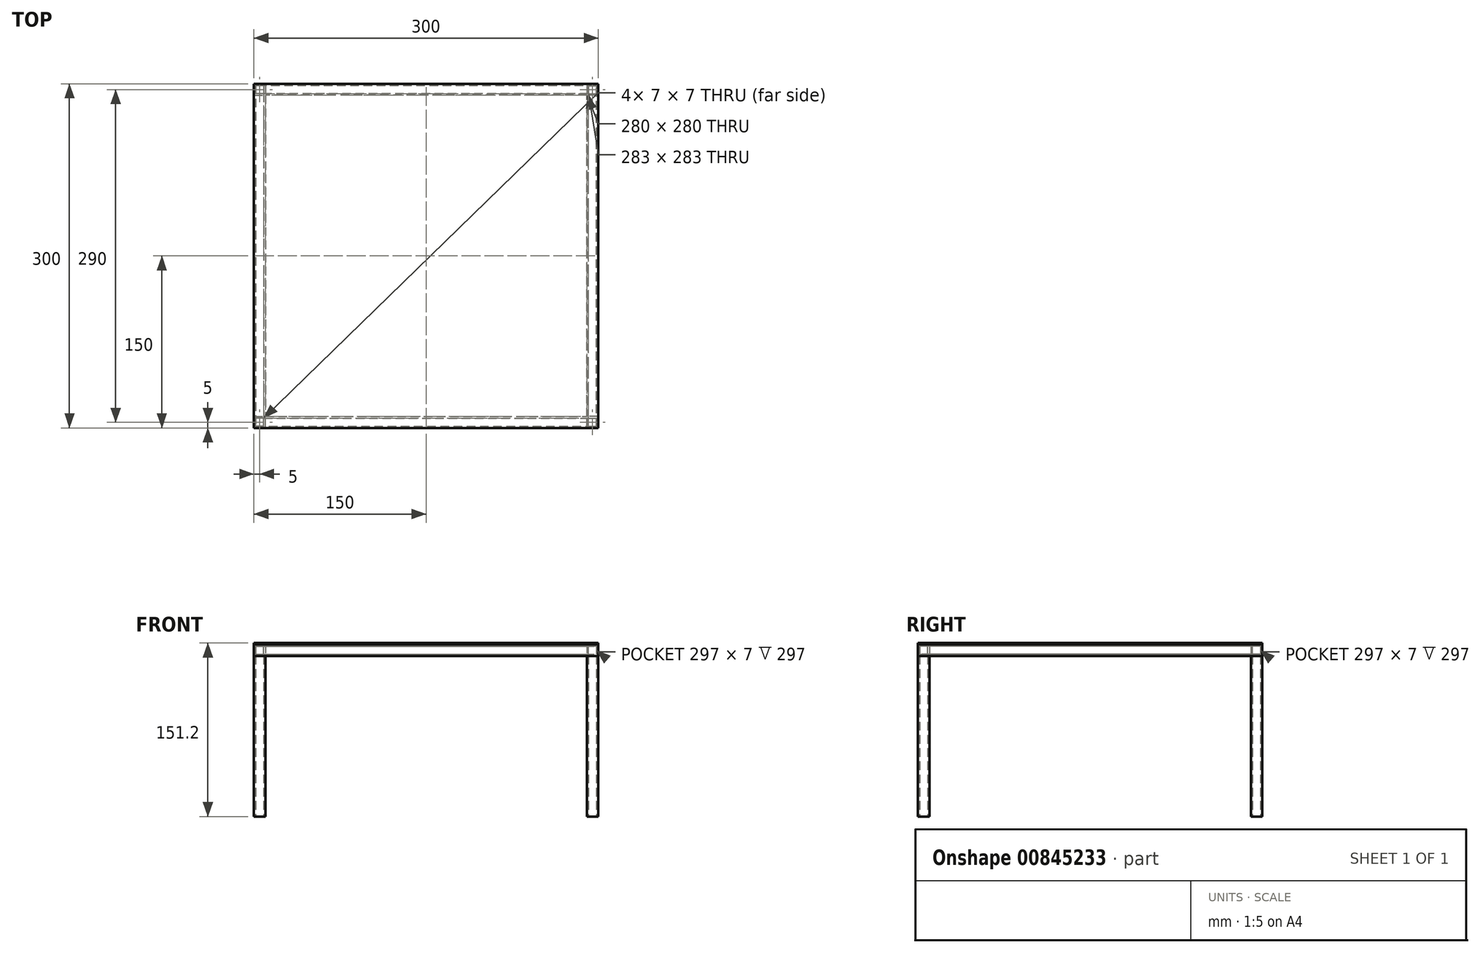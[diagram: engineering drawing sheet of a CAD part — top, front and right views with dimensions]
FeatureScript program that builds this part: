
annotation { "Feature Type Name" : "Feature", "Feature Type Description" : "" }
export const myFeature = defineFeature(function(context is Context, id is Id, definition is map)
    precondition{}
    {
        {
            var Q0;
            Q0=qCreatedBy(makeId("Top.planeOp"),FACE);
            var sketch = newSketch(context, id + "F0", { "sketchPlane" : qUnion([Q0])});
            skLineSegment(sketch, "E0.bottom", {"start": v(-150, 150) * mm, "end": v(-140, 150) * mm});
            skLineSegment(sketch, "E0.top", {"start": v(-150, 140) * mm, "end": v(-140, 140) * mm});
            skLineSegment(sketch, "E0.left", {"start": v(-150, 150) * mm, "end": v(-150, 140) * mm});
            skLineSegment(sketch, "E0.right", {"start": v(-140, 150) * mm, "end": v(-140, 140) * mm});
            skLineSegment(sketch, "E1.bottom", {"start": v(-141.5, 148.5) * mm, "end": v(-148.5, 148.5) * mm});
            skLineSegment(sketch, "E1.top", {"start": v(-141.5, 141.5) * mm, "end": v(-148.5, 141.5) * mm});
            skLineSegment(sketch, "E1.left", {"start": v(-141.5, 148.5) * mm, "end": v(-141.5, 141.5) * mm});
            skLineSegment(sketch, "E1.right", {"start": v(-148.5, 148.5) * mm, "end": v(-148.5, 141.5) * mm});
            skPoint(sketch, "E1.middle", {"position": v(-145, 145) * mm});
            skPoint(sketch, "E1.middle.positionSnap0", {"position": v(-145, 150) * mm});
            skPoint(sketch, "E1.middle.positionSnap1", {"position": v(-150, 145) * mm});
            skPoint(sketch, "E1.centerSnap0", {"position": v(-145, 150) * mm});
            skPoint(sketch, "E1.centerSnap1", {"position": v(-150, 145) * mm});
            skLineSegment(sketch, "E2.MirrorCS", {"start": v(150, 150) * mm, "end": v(140, 150) * mm});
            skLineSegment(sketch, "E3.MirrorCS", {"start": v(148.5, 148.5) * mm, "end": v(148.5, 141.5) * mm});
            skLineSegment(sketch, "E4.MirrorCS", {"start": v(150, 150) * mm, "end": v(150, 140) * mm});
            skLineSegment(sketch, "E5.MirrorCS", {"start": v(141.5, 148.5) * mm, "end": v(148.5, 148.5) * mm});
            skPoint(sketch, "E6.MirrorP", {"position": v(145, 150) * mm});
            skPoint(sketch, "E7.MirrorP", {"position": v(150, 145) * mm});
            skLineSegment(sketch, "E8.MirrorCS", {"start": v(141.5, 148.5) * mm, "end": v(141.5, 141.5) * mm});
            skLineSegment(sketch, "E9.MirrorCS", {"start": v(150, 140) * mm, "end": v(140, 140) * mm});
            skPoint(sketch, "E10.MirrorP", {"position": v(145, 145) * mm});
            skLineSegment(sketch, "E11.MirrorCS", {"start": v(140, 150) * mm, "end": v(140, 140) * mm});
            skLineSegment(sketch, "E12.MirrorCS", {"start": v(141.5, 141.5) * mm, "end": v(148.5, 141.5) * mm});
            skLineSegment(sketch, "E13.MirrorCS", {"start": v(141.5, -148.5) * mm, "end": v(141.5, -141.5) * mm});
            skLineSegment(sketch, "E14.MirrorCS", {"start": v(141.5, -148.5) * mm, "end": v(148.5, -148.5) * mm});
            skLineSegment(sketch, "E15.MirrorCS", {"start": v(140, -150) * mm, "end": v(140, -140) * mm});
            skLineSegment(sketch, "E16.MirrorCS", {"start": v(-141.5, -141.5) * mm, "end": v(-148.5, -141.5) * mm});
            skLineSegment(sketch, "E17.MirrorCS", {"start": v(-150, -150) * mm, "end": v(-140, -150) * mm});
            skLineSegment(sketch, "E18.MirrorCS", {"start": v(-150, -140) * mm, "end": v(-140, -140) * mm});
            skLineSegment(sketch, "E19.MirrorCS", {"start": v(-150, -150) * mm, "end": v(-150, -140) * mm});
            skLineSegment(sketch, "E20.MirrorCS", {"start": v(-148.5, -148.5) * mm, "end": v(-148.5, -141.5) * mm});
            skLineSegment(sketch, "E21.MirrorCS", {"start": v(-141.5, -148.5) * mm, "end": v(-141.5, -141.5) * mm});
            skLineSegment(sketch, "E22.MirrorCS", {"start": v(-141.5, -148.5) * mm, "end": v(-148.5, -148.5) * mm});
            skLineSegment(sketch, "E23.MirrorCS", {"start": v(150, -150) * mm, "end": v(140, -150) * mm});
            skLineSegment(sketch, "E24.MirrorCS", {"start": v(150, -150) * mm, "end": v(150, -140) * mm});
            skLineSegment(sketch, "E25.MirrorCS", {"start": v(148.5, -148.5) * mm, "end": v(148.5, -141.5) * mm});
            skLineSegment(sketch, "E26.MirrorCS", {"start": v(-140, -150) * mm, "end": v(-140, -140) * mm});
            skPoint(sketch, "E27.MirrorP", {"position": v(145, -150) * mm});
            skLineSegment(sketch, "E28.MirrorCS", {"start": v(150, -140) * mm, "end": v(140, -140) * mm});
            skLineSegment(sketch, "E29.MirrorCS", {"start": v(141.5, -141.5) * mm, "end": v(148.5, -141.5) * mm});
            skPoint(sketch, "E30.MirrorP", {"position": v(150, -145) * mm});
            skPoint(sketch, "E31.MirrorP", {"position": v(-145, -150) * mm});
            skPoint(sketch, "E32.MirrorP", {"position": v(-150, -145) * mm});
            skPoint(sketch, "E33.MirrorP", {"position": v(-145, -145) * mm});
            skPoint(sketch, "E34.MirrorP", {"position": v(145, -145) * mm});
            skSolve(sketch);
        }
        {
            var Q0;
            Q0=qSketchRegion(id+"F0",true);
            extrude(context, id + "F1", {"entities" : qUnion([Q0]), "depth" : 140 * mm, "offsetDistance" : 25 * mm});
        }
        {
            var Q0;
            Q0=makeQuery(id+"F1.opExtrude","CAP_FACE",FACE,{"disambiguationData":[OSD([sQuery(id+"F0.wireOp",EDGE,"E16.MirrorCS"),sQuery(id+"F0.wireOp",EDGE,"E17.MirrorCS"),sQuery(id+"F0.wireOp",EDGE,"E18.MirrorCS"),sQuery(id+"F0.wireOp",EDGE,"E19.MirrorCS"),sQuery(id+"F0.wireOp",EDGE,"E20.MirrorCS"),sQuery(id+"F0.wireOp",EDGE,"E21.MirrorCS"),sQuery(id+"F0.wireOp",EDGE,"E22.MirrorCS"),sQuery(id+"F0.wireOp",EDGE,"E26.MirrorCS")])],"isStart":false});
            var sketch = newSketch(context, id + "F2", { "sketchPlane" : qUnion([Q0])});
            skLineSegment(sketch, "E35.bottom", {"start": v(-150, 150) * mm, "end": v(150, 150) * mm});
            skLineSegment(sketch, "E35.top", {"start": v(-150, -150) * mm, "end": v(150, -150) * mm});
            skLineSegment(sketch, "E35.left", {"start": v(-150, 150) * mm, "end": v(-150, -150) * mm});
            skLineSegment(sketch, "E35.right", {"start": v(150, 150) * mm, "end": v(150, -150) * mm});
            skSolve(sketch);
        }
        {
            var Q0;
            Q0=qCreatedBy(makeId("Right.planeOp"),FACE);
            var sketch = newSketch(context, id + "F3", { "sketchPlane" : qUnion([Q0])});
            skLineSegment(sketch, "E36.bottom", {"start": v(-150, 140) * mm, "end": v(-140, 140) * mm});
            skLineSegment(sketch, "E36.top", {"start": v(-150, 150) * mm, "end": v(-140, 150) * mm});
            skLineSegment(sketch, "E36.left", {"start": v(-150, 140) * mm, "end": v(-150, 150) * mm});
            skLineSegment(sketch, "E36.right", {"start": v(-140, 140) * mm, "end": v(-140, 150) * mm});
            skLineSegment(sketch, "E37.bottom", {"start": v(-141.5, 148.5) * mm, "end": v(-148.5, 148.5) * mm});
            skLineSegment(sketch, "E37.top", {"start": v(-141.5, 141.5) * mm, "end": v(-148.5, 141.5) * mm});
            skLineSegment(sketch, "E37.left", {"start": v(-141.5, 148.5) * mm, "end": v(-141.5, 141.5) * mm});
            skLineSegment(sketch, "E37.right", {"start": v(-148.5, 148.5) * mm, "end": v(-148.5, 141.5) * mm});
            skPoint(sketch, "E37.middle", {"position": v(-145, 145) * mm});
            skPoint(sketch, "E37.middle.positionSnap0", {"position": v(-145, 150) * mm});
            skPoint(sketch, "E37.middle.positionSnap1", {"position": v(-150, 145) * mm});
            skPoint(sketch, "E37.centerSnap0", {"position": v(-145, 150) * mm});
            skPoint(sketch, "E37.centerSnap1", {"position": v(-150, 145) * mm});
            skSolve(sketch);
        }
        {
            var Q0;
            Q0=makeQuery(id+"F3.imprint","IMPRINT",FACE,{"disambiguationData":[TD([[makeQuery(id+"F3.imprint","IMPRINT",EDGE,{"derivedFrom":sQuery(id+"F3.wireOp",EDGE,"E36.bottom")}),1.0]])]});
            var Q1;
            Q1=sQuery(id+"F2.wireOp",EDGE,"E35.top");
            var Q2;
            Q2=sQuery(id+"F2.wireOp",EDGE,"E35.right");
            var Q3;
            Q3=sQuery(id+"F2.wireOp",EDGE,"E35.bottom");
            var Q4;
            Q4=sQuery(id+"F2.wireOp",EDGE,"E35.left");
            sweep(context, id + "F4", {"profiles" : qUnion([Q0]), "path" : qUnion([Q1, Q2, Q3, Q4])});
        }
        {
            var Q0;
            Q0=makeQuery(id+"F4.opSweep","SWEPT_FACE",FACE,{"disambiguationData":[OSD([sQuery(id+"F2.wireOp",EDGE,"E35.left"),sQuery(id+"F3.wireOp",EDGE,"E36.top")])]});
            var sketch = newSketch(context, id + "F5", { "sketchPlane" : qUnion([Q0])});
            skLineSegment(sketch, "E38.0", {"start": v(150, 150) * mm, "end": v(-150, 150) * mm});
            skLineSegment(sketch, "E38.1", {"start": v(150, -150) * mm, "end": v(150, 150) * mm});
            skLineSegment(sketch, "E38.2", {"start": v(-150, -150) * mm, "end": v(150, -150) * mm});
            skLineSegment(sketch, "E38.3", {"start": v(-150, 150) * mm, "end": v(-150, -150) * mm});
            skSolve(sketch);
        }
        {
            var Q0;
            Q0=qSketchRegion(id+"F5",true);
            extrude(context, id + "F6", {"entities" : qUnion([Q0]), "depth" : 1.2 * mm, "offsetDistance" : 25 * mm});
        }
    });
